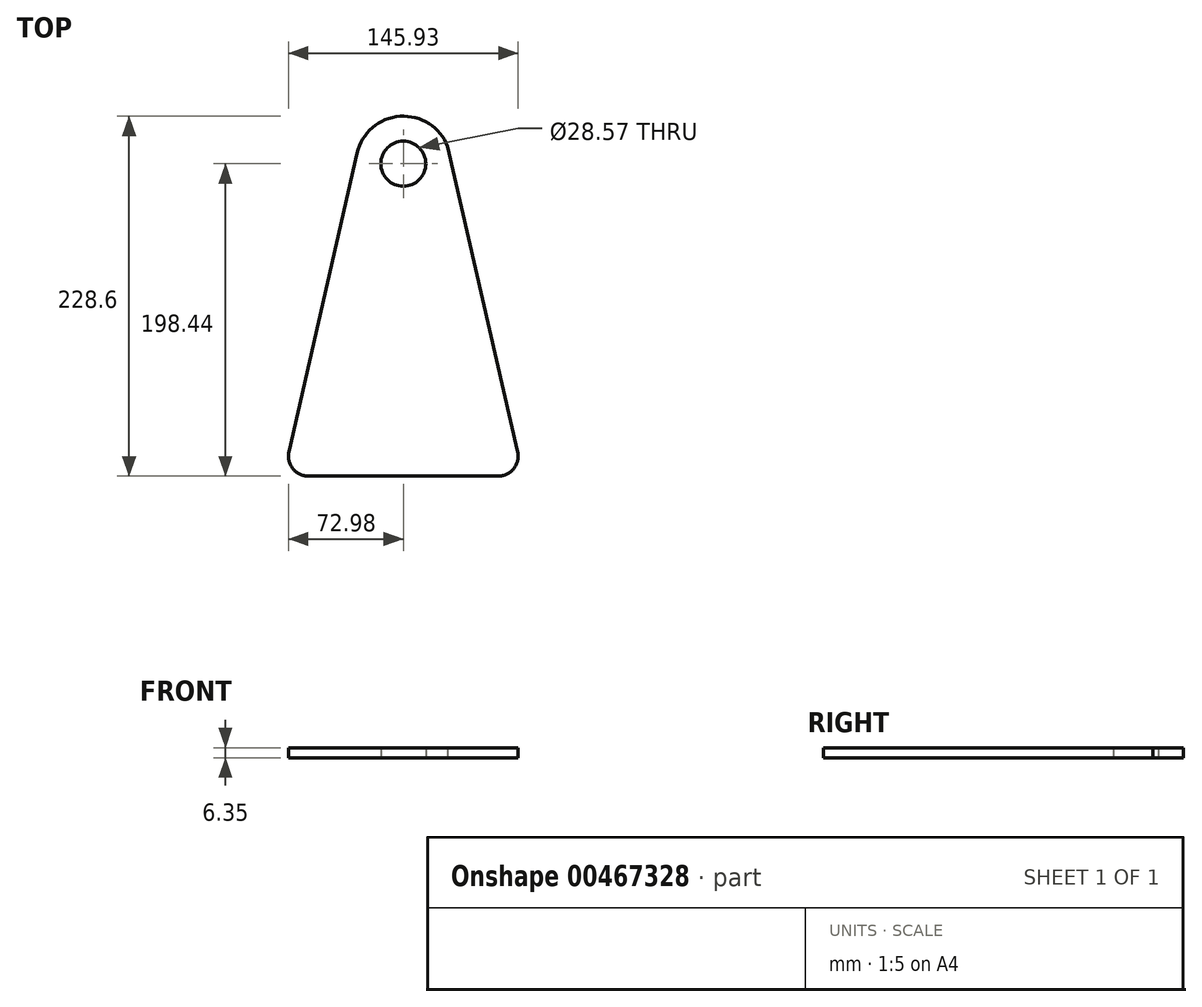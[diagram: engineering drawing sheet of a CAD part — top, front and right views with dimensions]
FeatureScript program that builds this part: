
annotation { "Feature Type Name" : "Feature", "Feature Type Description" : "" }
export const myFeature = defineFeature(function(context is Context, id is Id, definition is map)
    precondition{}
    {
        {
            var Q0;
            Q0=qCreatedBy(makeId("Top.planeOp"),FACE);
            var sketch = newSketch(context, id + "F0", { "sketchPlane" : qUnion([Q0])});
            skLineSegment(sketch, "E0", {"start": v(-60.28, -91.39) * mm, "end": v(60.25, -91.39) * mm});
            skCircle(sketch, "E1", {"center": v(0, 107.05) * mm, "radius": 14.29 * mm});
            skPoint(sketch, "E1.centerSnap0", {"position": v(0, -91.39) * mm});
            skLineSegment(sketch, "E2", {"start": v(-72.66, -75.86) * mm, "end": v(-29.4, 113.76) * mm});
            skArc(sketch, "E3.0", {"start": v(28.18, 117.8) * mm, "mid": v(-2.11, 137.14) * mm, "end": v(-29.4, 113.76) * mm});
            skLineSegment(sketch, "E4", {"start": v(28.18, 117.8) * mm, "end": v(72.63, -75.85) * mm});
            skPoint(sketch, "E5.visualSharp", {"position": v(-76.2, -91.39) * mm});
            skArc(sketch, "E5.filletArc", {"start": v(-72.66, -75.86) * mm, "mid": v(-70.2, -86.6) * mm, "end": v(-60.28, -91.39) * mm});
            skPoint(sketch, "E6.visualSharp", {"position": v(76.2, -91.39) * mm});
            skArc(sketch, "E6.filletArc", {"start": v(60.25, -91.39) * mm, "mid": v(70.19, -86.6) * mm, "end": v(72.63, -75.85) * mm});
            skSolve(sketch);
        }
        {
            var Q0;
            Q0=makeQuery(id+"F0.imprint","IMPRINT",FACE,{"disambiguationData":[TD([[makeQuery(id+"F0.imprint","IMPRINT",EDGE,{"derivedFrom":sQuery(id+"F0.wireOp",EDGE,"E0")}),1.0]])]});
            extrude(context, id + "F1", {"entities" : qUnion([Q0]), "depth" : 6.35 * mm, "offsetDistance" : 25.4 * mm});
        }
    });
